# Revit family: PRD_FrankeWS_WtrSpplFttngsFrWshBsnsAndTrghs_ElectronicPillarTap_F5EV1001-1008
name_source: partatom
category: Plumbing Fixtures
revit_build: Autodesk Revit 2018 (Build: 20190510_1515(x64)
units: mm (PartAtom-declared; Revit-internal decimal feet)

## family parameters
Always vertical = Yes
Cut with Voids When Loaded = No
OmniClass Number = 23.45.55.14
OmniClass Title = Single Faucets
Part Type = Normal
Room Calculation Point = No
Round Connector Dimension = Use Diameter
Shared = No
Work Plane-Based = No

## types (8) — shared parameters
AssetType = Fixed
Category = Pr_40_20_87_98, Washbasin taps
Color = Chrome
DefaultAutomaticHygieneFlushing = 24H-AFTER-ACTIVITY
Depressurised = no
DiameterNominal = 15 mm
DurationUnit = year
FaucetFunction = MIXED
FaucetMaterial = PRD_AR_ChromatedBrass_HighPolished
FaucetOperation = SELFCLOSING
FaucetType = PILLAR
Features = For sanitary facilities. For connection to pre-mixed hot or cold water, high-polished chromium-plated brass.
Finish = high-polished chromium-plated brass
FlowColdWater = 0.1 L/s
FlowRateMaximum = 0.08 L/s at 3 bar
FunctionalPrinciple = electronic self-closing
HygieneFlushing = yes
IfcExportAs = IfcValveType
IfcExportType = FAUCET
InletSize = G3-8
Manufacturer = KWC Group AG
ManufacturerName = KWC Group AG
ManufacturerURL = www.kwc.com
Material = Brass
MaterialsBody = Brass
MinimumFlowPressure = 1.00 bar
NBSDescription = Water supply fittings for wash basins and troughs
NBSReference = 45-35-70/371
NominalHeight = 140 mm  [stored 0.459318 ft]
NominalWidth = 60 mm  [stored 0.19685 ft]
OutletMaterial = PRD_AR_SyntheticGrey
PowerConsumption = 1.5
ProductInformation = https://pim.kwc.com
ProtectiveShutdown = yes
SensorMaterial = PRD_AR_SyntheticDarkGrey
SideSensorMaterial = PRD_AR_SyntheticDarkBlue
SoundInsulation = no
SpoutProjection = 125.00 mm
ThermalDisinfection = no
TypeOfMixing = no mixing
TypeOfMounting = taphole
TypeOfOperation = sensor operation
TypeOfSensor = opto-electronic sensor
TypeOfTap = pillar tap
URL = www.kwc.com
Uniclass2015Code = Pr_40_20_87_98
Uniclass2015Title = Washbasin taps
Uniclass2015Version = Products v1.10
Version = 1
WarrantyDurationUnit = year
zero-valued in all types: NominalLength

## per-type parameters (varying)
| type | BIMObjectName | Description | GrossWeight | Model | ModelNumber | ModelReference | Name | NetWeight | PositionOfPowerConnection | PowerSupplyConnection | ProtectiveSystemIP | VolumeFlowRate |
| F5EV1001 - 0.08 L/s with 6 V lithium battery | PRD_AR_WaterSupplyFittingsForWashBasinsAndTroughs_ElectronicPillarTap_F5EV1001 | F5E pillar tap DN 15 for sanitary facilities, opto-electronically controlled. For connection to pre-mixed hot or cold water via hose and strainer. Control electronics, solenoid valve cartridge, 6 V lithium battery (CR-P2) and sensor in all-metal housing, high-polished chromium-plated brass. Anti-theft aerator, design SLIM, with integrated flow regulator 5.0 l/min. Activated water hygiene flushing 24 hours after last activation, safety switch-off with continuous reflection and saving of statistical data. With option for parameterization and communication via optional, bidirectional remote control. | 1.70 kg | F5EV1001 | 2030027922 | F5EV1001 | F5 electronic pillar tap F5EV1001 | 1.62 kg |  | Battery 6 V | IP59K | 0.08 L/s at 3 bar |
| F5EV1002 - 0.08 L/s with 100 - 240 V AC plug-in power supply unit | PRD_AR_WaterSupplyFittingsForWashBasinsAndTroughs_ElectronicPillarTap_F5EV1002 | F5E pillar tap DN 15 for sanitary facilities, opto-electronically controlled. For connection to pre-mixed hot or cold water via hose and strainer. Control electronics, solenoid valve cartridge and sensor in all-metal housing, high-polished chromium-plated brass. Anti-theft aerator, design SLIM, with integrated flow regulator 5.0 l/min. Activated water hygiene flushing 24 hours after last activation, safety switch-off with continuous reflection and saving of statistical data. With option for parameterization and communication via optional, bidirectional remote control. With 100 - 240 V AC plug-in power supply unit. | 1.80 kg | F5EV1002 | 2030035330 | F5EV1002 | F5 electronic pillar tap F5EV1002 | 1.72 kg | from bottom | 100 - 240 V AC | tap IP59K | 0.08 L/s at 3 bar |
| F5EV1003 - 0.08 L/s with in-wall power supply 100 - 240 V AC | PRD_AR_WaterSupplyFittingsForWashBasinsAndTroughs_ElectronicPillarTap_F5EV1003 | F5E pillar tap DN 15 for sanitary facilities, opto-electronically controlled. For connection to pre-mixed hot or cold water via hose and strainer. Control electronics, solenoid valve cartridge and sensor in all-metal housing, high-polished chromium-plated brass. Anti-theft aerator, design SLIM, with integrated flow regulator 5.0 l/min. Activated water hygiene flushing 24 hours after last activation, safety switch-off with continuous reflection and saving of statistical data. With option for parameterization and communication via optional, bidirectional remote control. With in-wall power supply 100 - 240 V AC. | 1.90 kg | F5EV1003 | 2030035331 | F5EV1003 | F5 electronic pillar tap F5EV1003 | 1.81 kg | from bottom | 100 - 240 V AC | tap IP59K | 0.08 L/s at 3 bar |
| F5EV1004 - 0.08 L/s with separate power supply via power supply unit 6.75 V / 12 V DC | PRD_AR_WaterSupplyFittingsForWashBasinsAndTroughs_ElectronicPillarTap_F5EV1004 | F5E pillar tap DN 15 for sanitary facilities, opto-electronically controlled. For connection to pre-mixed hot or cold water via hose and strainer. Control electronics, solenoid valve cartridge and sensor in all-metal housing, high-polished chromium-plated brass. Anti-theft aerator, design SLIM, with integrated flow regulator 5.0 l/min. Activated water hygiene flushing 24 hours after last activation, safety switch-off with continuous reflection and saving of statistical data. With option for parameterization and communication via optional, bidirectional remote control. Separate power supply via power supply unit 6.75 V / 12 V DC or AQUA 3000 open system accessories. | 1.70 kg | F5EV1004 | 2030036158 | F5EV1004 | F5 electronic pillar tap F5EV1004 | 1.60 kg | from bottom | 6,75 / 12 V DC / A3000 open | IP59K | 0.08 L/s at 3 bar |
| F5EV1005 - 0.05 L/s with 6 V lithium battery | PRD_AR_WaterSupplyFittingsForWashBasinsAndTroughs_ElectronicPillarTap_F5EV1005 | F5E pillar tap DN 15 for sanitary facilities, opto-electronically controlled. For connection to pre-mixed hot or cold water via hose and strainer. Control electronics, solenoid valve cartridge, 6 V lithium battery (CR-P2) and sensor in all-metal housing, high-polished chromium-plated brass. Aerator with integrated flow regulator 3.0 l/min. Activated water hygiene flushing 24 hours after last activation, safety switch-off with continuous reflection and saving of statistical data. With option for parameterization and communication via optional, bidirectional remote control. | 1.80 kg | F5EV1005 | 2030039435 | F5EV1005 | F5 electronic pillar tap F5EV1005 | 1.71 kg |  | Battery 6 V | IP59K | 0.05 L/s at 3 bar |
| F5EV1006 - 0.05 L/s with 100 - 240 V AC plug-in power supply unit | PRD_AR_WaterSupplyFittingsForWashBasinsAndTroughs_ElectronicPillarTap_F5EV1006 | F5E pillar tap DN 15 for sanitary facilities, opto-electronically controlled. For connection to pre-mixed hot or cold water via hose and strainer. Control electronics, solenoid valve cartridge and sensor in all-metal housing, high-polished chromium-plated brass. Aerator with integrated flow regulator 3.0 l/min. Activated water hygiene flushing 24 hours after last activation, safety switch-off with continuous reflection and saving of statistical data. With option for parameterization and communication via optional, bidirectional remote control. With 100 - 240 V AC plug-in power supply unit. | 1.90 kg | F5EV1006 | 2030039436 | F5EV1006 | F5 electronic pillar tap F5EV1006 | 1.81 kg | from bottom | 100 - 240 V AC | tap IP59K | 0.05 L/s at 3 bar |
| F5EV1007 - 0.05 L/s with in-wall power supply 100 - 240 V AC | PRD_AR_WaterSupplyFittingsForWashBasinsAndTroughs_ElectronicPillarTap_F5EV1007 | F5E pillar tap DN 15 for sanitary facilities, opto-electronically controlled. For connection to pre-mixed hot or cold water via hose and strainer. Control electronics, solenoid valve cartridge and sensor in all-metal housing, high-polished chromium-plated brass. Aerator with integrated flow regulator 3.0 l/min. Activated water hygiene flushing 24 hours after last activation, safety switch-off with continuous reflection and saving of statistical data. With option for parameterization and communication via optional, bidirectional remote control. With in-wall power supply 100 - 240 V AC. | 1.90 kg | F5EV1007 | 2030039437 | F5EV1007 | F5 electronic pillar tap F5EV1007 | 1.81 kg | from bottom | 100 - 240 V AC | tap IP59K | 0.05 L/s at 3 bar |
| F5EV1008 - 0.05 L/s with separate power supply via power supply unit 6.75 V / 12 V DC | PRD_AR_WaterSupplyFittingsForWashBasinsAndTroughs_ElectronicPillarTap_F5EV1008 | F5E pillar tap DN 15 for sanitary facilities, opto-electronically controlled. For connection to pre-mixed hot or cold water via hose and strainer. Control electronics, solenoid valve cartridge and sensor in all-metal housing, high-polished chromium-plated brass. Aerator with integrated flow regulator 3.0 l/min. Activated water hygiene flushing 24 hours after last activation, safety switch-off with continuous reflection and saving of statistical data. With option for parameterization and communication via optional, bidirectional remote control. Separate power supply via power supply unit 6.75 V / 12 V DC or AQUA 3000 open system accessories. | 1.70 kg | F5EV1008 | 2030039438 | F5EV1008 | F5 electronic pillar tap F5EV1008 | 1.62 kg | from bottom | 6,75 / 12 V DC / A3000 open | IP59K | 0.05 L/s at 3 bar |

note: [stored X ft] marks values corroborated as IEEE doubles in the binary element streams (Revit-internal decimal feet)

## geometry (parser evidence)
native form markers: Sweep x2
no freeform markers — native parametric forms only
